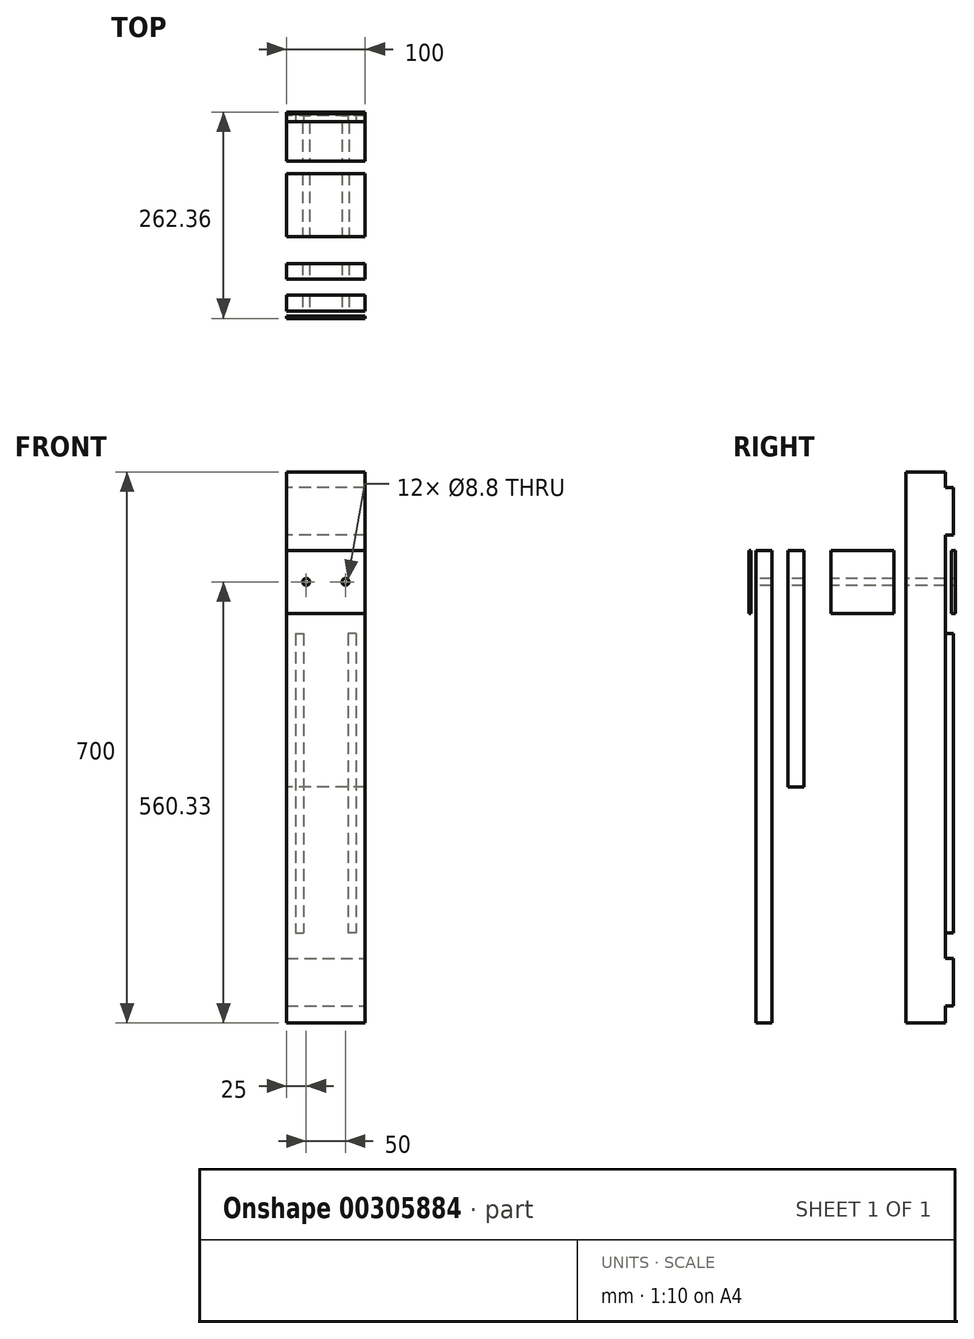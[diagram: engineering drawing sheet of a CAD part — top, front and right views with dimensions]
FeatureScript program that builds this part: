
annotation { "Feature Type Name" : "Feature", "Feature Type Description" : "" }
export const myFeature = defineFeature(function(context is Context, id is Id, definition is map)
    precondition{}
    {
        {
            var Q0;
            Q0=qCreatedBy(makeId("Front.planeOp"),FACE);
            var sketch = newSketch(context, id + "F0", { "sketchPlane" : qUnion([Q0])});
            skLineSegment(sketch, "E0.bottom", {"start": v(-50, 40) * mm, "end": v(50, 40) * mm});
            skLineSegment(sketch, "E0.top", {"start": v(-50, -40) * mm, "end": v(50, -40) * mm});
            skLineSegment(sketch, "E0.left", {"start": v(-50, 40) * mm, "end": v(-50, -40) * mm});
            skLineSegment(sketch, "E0.right", {"start": v(50, 40) * mm, "end": v(50, -40) * mm});
            skPoint(sketch, "E1", {"position": v(-25, 0) * mm});
            skPoint(sketch, "E2.MirrorP", {"position": v(25, 0) * mm});
            skSolve(sketch);
        }
        {
            var Q0;
            Q0 = qSketchRegion(id + "F0", true);
            extrude(context, id + "F1", {"entities" : qUnion([Q0]), "depth" : 3 * mm});
        }
        {
            var Q0;
            Q0=qCreatedBy(makeId("Right.planeOp"),FACE);
            var sketch = newSketch(context, id + "F2", { "sketchPlane" : qUnion([Q0])});
            skLineSegment(sketch, "E3.bottom", {"start": v(6.42, 39.67) * mm, "end": v(26.42, 39.67) * mm});
            skLineSegment(sketch, "E3.top", {"start": v(6.42, -560.33) * mm, "end": v(26.42, -560.33) * mm});
            skLineSegment(sketch, "E3.left", {"start": v(6.42, 39.67) * mm, "end": v(6.42, -560.33) * mm});
            skLineSegment(sketch, "E3.right", {"start": v(26.42, 39.67) * mm, "end": v(26.42, -560.33) * mm});
            skLineSegment(sketch, "E4.bottom", {"start": v(101.26, 39.67) * mm, "end": v(181.26, 39.67) * mm});
            skLineSegment(sketch, "E4.top", {"start": v(101.26, -40.33) * mm, "end": v(181.26, -40.33) * mm});
            skLineSegment(sketch, "E4.left", {"start": v(101.26, 39.67) * mm, "end": v(101.26, -40.33) * mm});
            skLineSegment(sketch, "E4.right", {"start": v(181.26, 39.67) * mm, "end": v(181.26, -40.33) * mm});
            skLineSegment(sketch, "E5.bottom", {"start": v(196.86, 139.67) * mm, "end": v(246.86, 139.67) * mm});
            skLineSegment(sketch, "E5.top", {"start": v(196.86, -560.33) * mm, "end": v(246.86, -560.33) * mm});
            skLineSegment(sketch, "E5.left", {"start": v(196.86, 139.67) * mm, "end": v(196.86, -560.33) * mm});
            skLineSegment(sketch, "E5.right", {"start": v(246.86, 139.67) * mm, "end": v(246.86, -560.33) * mm});
            skPoint(sketch, "E6", {"position": v(196.86, -40.33) * mm});
            skPoint(sketch, "E7", {"position": v(196.86, 39.67) * mm});
            skPoint(sketch, "E8", {"position": v(26.42, -40.33) * mm});
            skPoint(sketch, "E9", {"position": v(101.26, 39.67) * mm});
            skPoint(sketch, "E10", {"position": v(0, 39.67) * mm});
            skPoint(sketch, "E11", {"position": v(6.42, -40.33) * mm});
            skPoint(sketch, "E12", {"position": v(0, -40.33) * mm});
            skPoint(sketch, "E13", {"position": v(246.86, 39.67) * mm});
            skPoint(sketch, "E14", {"position": v(246.86, -40.33) * mm});
            skLineSegment(sketch, "E15.bottom", {"start": v(254.36, 39.67) * mm, "end": v(259.36, 39.67) * mm});
            skLineSegment(sketch, "E15.top", {"start": v(254.36, -40.33) * mm, "end": v(259.36, -40.33) * mm});
            skLineSegment(sketch, "E15.left", {"start": v(254.36, 39.67) * mm, "end": v(254.36, -40.33) * mm});
            skLineSegment(sketch, "E15.right", {"start": v(259.36, 39.67) * mm, "end": v(259.36, -40.33) * mm});
            skPoint(sketch, "E16", {"position": v(26.42, -260.33) * mm});
            skLineSegment(sketch, "E17.bottom", {"start": v(46.92, 39.67) * mm, "end": v(66.92, 39.67) * mm});
            skLineSegment(sketch, "E17.top", {"start": v(46.92, -260.33) * mm, "end": v(66.92, -260.33) * mm});
            skLineSegment(sketch, "E17.left", {"start": v(46.92, 39.67) * mm, "end": v(46.92, -260.33) * mm});
            skLineSegment(sketch, "E17.right", {"start": v(66.92, 39.67) * mm, "end": v(66.92, -260.33) * mm});
            skPoint(sketch, "E18", {"position": v(196.86, 59.67) * mm});
            skPoint(sketch, "E19", {"position": v(196.86, 119.67) * mm});
            skPoint(sketch, "E20", {"position": v(246.86, 119.67) * mm});
            skPoint(sketch, "E21", {"position": v(246.86, 59.67) * mm});
            skPoint(sketch, "E22", {"position": v(196.86, -550.33) * mm});
            skPoint(sketch, "E23", {"position": v(246.86, -550.33) * mm});
            skPoint(sketch, "E24", {"position": v(246.86, -490.33) * mm});
            skPoint(sketch, "E25", {"position": v(196.86, -490.33) * mm});
            skSolve(sketch);
        }
        {
            var Q0;
            Q0=makeQuery(id+"F2.imprint","IMPRINT",FACE,{"disambiguationData":[TD([[makeQuery(id+"F2.imprint","IMPRINT",EDGE,{"derivedFrom":sQuery(id+"F2.wireOp",EDGE,"E3.bottom")}),-1.0]])]});
            var Q1;
            Q1=makeQuery(id+"F2.imprint","IMPRINT",FACE,{"disambiguationData":[TD([[makeQuery(id+"F2.imprint","IMPRINT",EDGE,{"derivedFrom":sQuery(id+"F2.wireOp",EDGE,"E4.bottom")}),-1.0]])]});
            var Q2;
            Q2=makeQuery(id+"F2.imprint","IMPRINT",FACE,{"disambiguationData":[TD([[makeQuery(id+"F2.imprint","IMPRINT",EDGE,{"derivedFrom":sQuery(id+"F2.wireOp",EDGE,"E5.bottom")}),-1.0]])]});
            var Q3;
            Q3=makeQuery(id+"F2.imprint","IMPRINT",FACE,{"disambiguationData":[TD([[makeQuery(id+"F2.imprint","IMPRINT",EDGE,{"derivedFrom":sQuery(id+"F2.wireOp",EDGE,"E15.bottom")}),-1.0]])]});
            var Q4;
            Q4=makeQuery(id+"F2.imprint","IMPRINT",FACE,{"disambiguationData":[TD([[makeQuery(id+"F2.imprint","IMPRINT",EDGE,{"derivedFrom":sQuery(id+"F2.wireOp",EDGE,"E17.bottom")}),-1.0]])]});
            extrude(context, id + "F3", {"entities" : qUnion([Q0, Q1, Q2, Q3, Q4]), "depth" : 100 * mm, "symmetric" : true});
        }
        {
            var Q0;
            Q0=sQuery(id+"F0.wireOp",VERTEX,"E1");
            var Q1;
            Q1=sQuery(id+"F0.wireOp",VERTEX,"E2.MirrorP");
            var Q2;
            Q2=makeQuery(id+"F3.opExtrude","SWEPT_BODY",BODY,{"disambiguationData":[OSD([sQuery(id+"F2.wireOp",EDGE,"E3.bottom"),sQuery(id+"F2.wireOp",EDGE,"E3.top"),sQuery(id+"F2.wireOp",EDGE,"E3.left"),sQuery(id+"F2.wireOp",EDGE,"E3.right")])]});
            var Q3;
            Q3=makeQuery(id+"F3.opExtrude","SWEPT_BODY",BODY,{"disambiguationData":[OSD([sQuery(id+"F2.wireOp",EDGE,"E5.bottom"),sQuery(id+"F2.wireOp",EDGE,"E5.top"),sQuery(id+"F2.wireOp",EDGE,"E5.left"),sQuery(id+"F2.wireOp",EDGE,"E5.right")])]});
            var Q4;
            Q4=makeQuery(id+"F3.opExtrude","SWEPT_BODY",BODY,{"disambiguationData":[OSD([sQuery(id+"F2.wireOp",EDGE,"E4.bottom"),sQuery(id+"F2.wireOp",EDGE,"E4.top"),sQuery(id+"F2.wireOp",EDGE,"E4.left"),sQuery(id+"F2.wireOp",EDGE,"E4.right")])]});
            var Q5;
            Q5=makeQuery(id+"F3.opExtrude","SWEPT_BODY",BODY,{"disambiguationData":[OSD([sQuery(id+"F2.wireOp",EDGE,"E15.bottom"),sQuery(id+"F2.wireOp",EDGE,"E15.top"),sQuery(id+"F2.wireOp",EDGE,"E15.left"),sQuery(id+"F2.wireOp",EDGE,"E15.right")])]});
            var Q6;
            Q6=makeQuery(id+"F3.opExtrude","SWEPT_BODY",BODY,{"disambiguationData":[OSD([sQuery(id+"F2.wireOp",EDGE,"E17.bottom"),sQuery(id+"F2.wireOp",EDGE,"E17.top"),sQuery(id+"F2.wireOp",EDGE,"E17.left"),sQuery(id+"F2.wireOp",EDGE,"E17.right")])]});
            var Q7;
            Q7=makeQuery(id+"F1.opExtrude","SWEPT_BODY",BODY,{"disambiguationData":[OSD([sQuery(id+"F0.wireOp",EDGE,"E0.bottom"),sQuery(id+"F0.wireOp",EDGE,"E0.top"),sQuery(id+"F0.wireOp",EDGE,"E0.left"),sQuery(id+"F0.wireOp",EDGE,"E0.right")])]});
            hole(context, id + "F4", {"style" : HoleStyle.SIMPLE, "endStyle" : HoleEndStyle.THROUGH, "standardTappedOrClearance" : lookupTablePath({ "standard" : "ISO", "fit" : "Normal", "size" : "M8", "type" : "Clearance" }), "standardBlindInLast" : lookupTablePath({ "fit" : "Standard", "standard" : "ISO", "size" : "M8", "type" : "Clearance" }), "holeDiameter" : 8.8 * mm, "tappedDepth" : 12 * mm, "tapClearance" : 3, "locations" : qUnion([Q0, Q1]), "scope" : qUnion([Q2, Q3, Q4, Q5, Q6, Q7])});
        }
        {
            var Q0;
            Q0=sQuery(id+"F0.wireOp",VERTEX,"E1");
            var Q1;
            Q1=sQuery(id+"F0.wireOp",VERTEX,"E2.MirrorP");
            var Q2;
            Q2=makeQuery(id+"F1.opExtrude","SWEPT_BODY",BODY,{"disambiguationData":[OSD([sQuery(id+"F0.wireOp",EDGE,"E0.bottom"),sQuery(id+"F0.wireOp",EDGE,"E0.top"),sQuery(id+"F0.wireOp",EDGE,"E0.left"),sQuery(id+"F0.wireOp",EDGE,"E0.right")])]});
            hole(context, id + "F5", {"style" : HoleStyle.SIMPLE, "endStyle" : HoleEndStyle.THROUGH, "oppositeDirection" : true, "standardTappedOrClearance" : lookupTablePath({ "standard" : "ISO", "fit" : "Normal", "size" : "M8", "type" : "Clearance" }), "standardBlindInLast" : lookupTablePath({ "fit" : "Standard", "standard" : "ISO", "size" : "M8", "type" : "Clearance" }), "holeDiameter" : 8.8 * mm, "tappedDepth" : 12 * mm, "tapClearance" : 3, "locations" : qUnion([Q0, Q1]), "scope" : qUnion([Q2])});
        }
        {
            var Q0;
            Q0=makeQuery(id+"F3.opExtrude","SWEPT_FACE",FACE,{"disambiguationData":[OSD([sQuery(id+"F2.wireOp",EDGE,"E5.right")])]});
            var sketch = newSketch(context, id + "F6", { "sketchPlane" : qUnion([Q0])});
            skLineSegment(sketch, "E26.bottom", {"start": v(-38.42, -65.77) * mm, "end": v(-28.42, -65.77) * mm});
            skLineSegment(sketch, "E26.top", {"start": v(-38.42, -446.12) * mm, "end": v(-28.42, -446.12) * mm});
            skLineSegment(sketch, "E26.left", {"start": v(-38.42, -65.77) * mm, "end": v(-38.42, -446.12) * mm});
            skLineSegment(sketch, "E26.right", {"start": v(-28.42, -65.77) * mm, "end": v(-28.42, -446.12) * mm});
            skLineSegment(sketch, "E27.MirrorCS", {"start": v(28.42, -65.77) * mm, "end": v(28.42, -446.12) * mm});
            skLineSegment(sketch, "E28.MirrorCS", {"start": v(38.42, -65.77) * mm, "end": v(38.42, -446.12) * mm});
            skLineSegment(sketch, "E29.MirrorCS", {"start": v(38.42, -65.77) * mm, "end": v(28.42, -65.77) * mm});
            skLineSegment(sketch, "E30.MirrorCS", {"start": v(38.42, -446.12) * mm, "end": v(28.42, -446.12) * mm});
            skLineSegment(sketch, "E31.bottom", {"start": v(-50, 119.69) * mm, "end": v(50, 119.69) * mm});
            skLineSegment(sketch, "E31.top", {"start": v(-50, 59.69) * mm, "end": v(50, 59.69) * mm});
            skLineSegment(sketch, "E31.left", {"start": v(-50, 119.69) * mm, "end": v(-50, 59.69) * mm});
            skLineSegment(sketch, "E31.right", {"start": v(50, 119.69) * mm, "end": v(50, 59.69) * mm});
            skLineSegment(sketch, "E32.bottom", {"start": v(50, -478.63) * mm, "end": v(-50, -478.63) * mm});
            skLineSegment(sketch, "E32.top", {"start": v(50, -538.63) * mm, "end": v(-50, -538.63) * mm});
            skLineSegment(sketch, "E32.left", {"start": v(50, -478.63) * mm, "end": v(50, -538.63) * mm});
            skLineSegment(sketch, "E32.right", {"start": v(-50, -478.63) * mm, "end": v(-50, -538.63) * mm});
            skSolve(sketch);
        }
        {
            var Q0;
            Q0=makeQuery(id+"F6.imprint","IMPRINT",FACE,{"disambiguationData":[TD([[makeQuery(id+"F6.imprint","IMPRINT",EDGE,{"derivedFrom":sQuery(id+"F6.wireOp",EDGE,"E27.MirrorCS")}),1.0]])]});
            var Q1;
            Q1=makeQuery(id+"F6.imprint","IMPRINT",FACE,{"disambiguationData":[TD([[makeQuery(id+"F6.imprint","IMPRINT",EDGE,{"derivedFrom":sQuery(id+"F6.wireOp",EDGE,"E26.bottom")}),-1.0]])]});
            var Q2;
            Q2=makeQuery(id+"F6.imprint","IMPRINT",FACE,{"disambiguationData":[TD([[makeQuery(id+"F6.imprint","IMPRINT",EDGE,{"derivedFrom":sQuery(id+"F6.wireOp",EDGE,"E31.bottom")}),-1.0]])]});
            var Q3;
            Q3=makeQuery(id+"F6.imprint","IMPRINT",FACE,{"disambiguationData":[TD([[makeQuery(id+"F6.imprint","IMPRINT",EDGE,{"derivedFrom":sQuery(id+"F6.wireOp",EDGE,"E32.bottom")}),1.0]])]});
            extrude(context, id + "F7", {"entities" : qUnion([Q0, Q1, Q2, Q3]), "operationType" : NewBodyOperationType.ADD, "depth" : 10 * mm});
        }
    });
